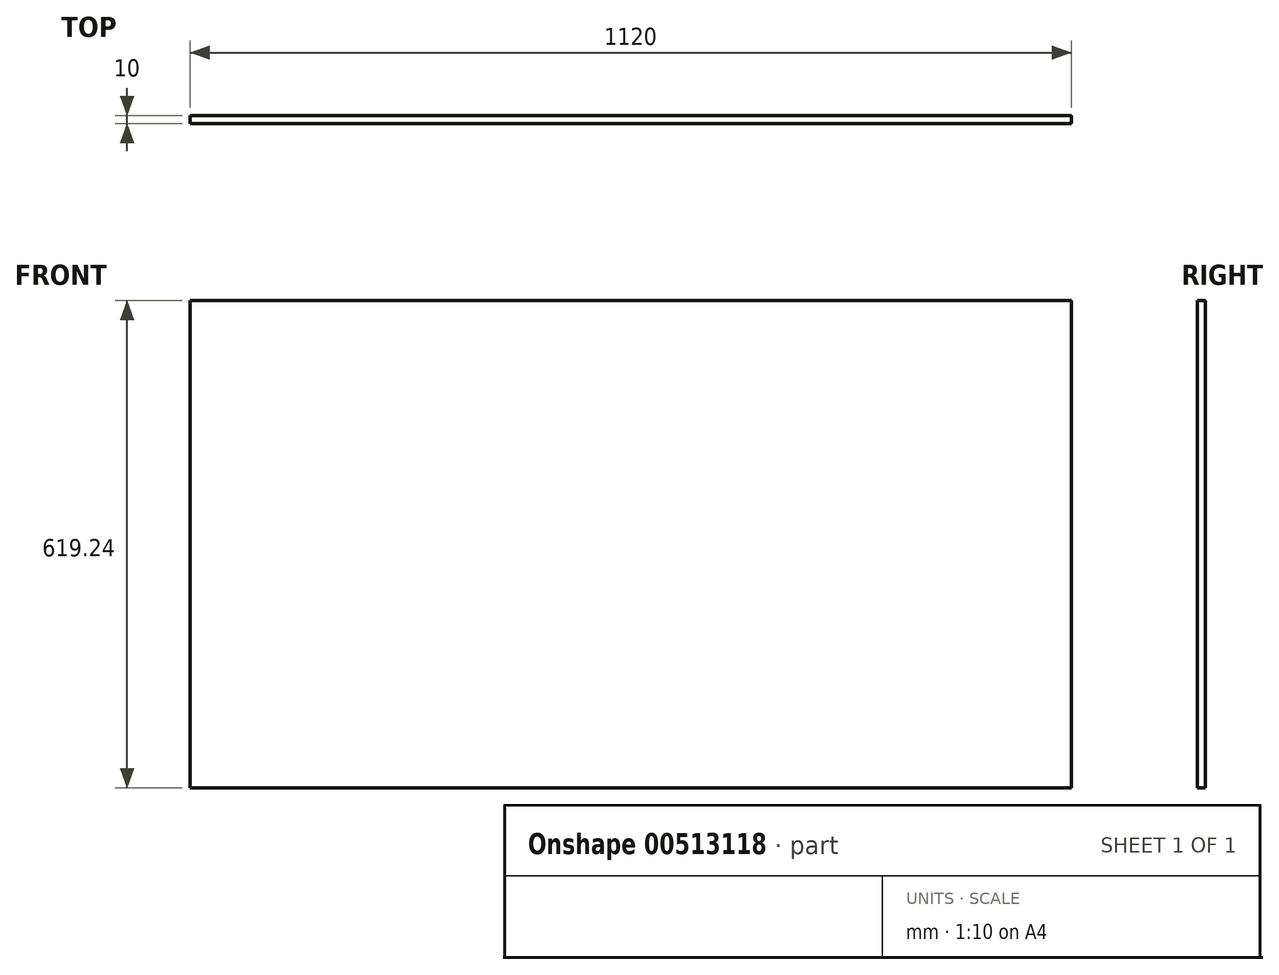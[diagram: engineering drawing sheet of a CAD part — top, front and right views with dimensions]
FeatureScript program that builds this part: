
annotation { "Feature Type Name" : "Feature", "Feature Type Description" : "" }
export const myFeature = defineFeature(function(context is Context, id is Id, definition is map)
    precondition{}
    {
        {
            var Q0;
            Q0=qCreatedBy(makeId("Front.planeOp"),FACE);
            var sketch = newSketch(context, id + "F0", { "sketchPlane" : qUnion([Q0])});
            skLineSegment(sketch, "E0.bottom", {"start": v(-635.84, -266.8) * mm, "end": v(464.16, -266.8) * mm});
            skLineSegment(sketch, "E0.top", {"start": v(-635.84, -866.04) * mm, "end": v(464.16, -866.04) * mm});
            skLineSegment(sketch, "E0.left", {"start": v(-635.84, -266.8) * mm, "end": v(-635.84, -866.04) * mm});
            skLineSegment(sketch, "E0.right", {"start": v(464.16, -266.8) * mm, "end": v(464.16, -866.04) * mm});
            skSolve(sketch);
        }
        {
            var Q0;
            Q0=makeQuery(id+"F0.imprint","IMPRINT",FACE,{"disambiguationData":[TD([[makeQuery(id+"F0.imprint","IMPRINT",EDGE,{"derivedFrom":sQuery(id+"F0.wireOp",EDGE,"E0.bottom")}),-1.0]])]});
            extrude(context, id + "F1", {"entities" : qUnion([Q0]), "depth" : 10 * mm, "offsetDistance" : 25 * mm});
        }
        {
            var Q0;
            Q0=makeQuery(id+"F1.opExtrude","SWEPT_FACE",FACE,{"disambiguationData":[OSD([sQuery(id+"F0.wireOp",EDGE,"E0.bottom")])]});
            extrude(context, id + "F2", {"entities" : qUnion([Q0]), "operationType" : NewBodyOperationType.ADD, "depth" : 10 * mm, "offsetDistance" : 25 * mm});
        }
        {
            var Q0;
            {var subQ0=sQuery(id+"F0.wireOp",EDGE,"E0.left");Q0=makeQuery(id+"F2.boolean.opBoolean","MERGE",FACE,{"derivedFrom":[makeQuery(id+"F1.opExtrude","SWEPT_FACE",FACE,{"disambiguationData":[OSD([subQ0])]}),makeQuery(id+"F2.opExtrude","SWEPT_FACE",FACE,{"disambiguationData":[OSD([sQuery(id+"F0.wireOp",EDGE,"E0.bottom"),subQ0])]})]});}
            extrude(context, id + "F3", {"entities" : qUnion([Q0]), "operationType" : NewBodyOperationType.ADD, "depth" : 10 * mm, "offsetDistance" : 25 * mm});
        }
        {
            var Q0;
            {var subQ0=sQuery(id+"F0.wireOp",EDGE,"E0.top");Q0=makeQuery(id+"F3.boolean.opBoolean","MERGE",FACE,{"derivedFrom":[makeQuery(id+"F1.opExtrude","SWEPT_FACE",FACE,{"disambiguationData":[OSD([subQ0])]}),makeQuery(id+"F3.opExtrude","SWEPT_FACE",FACE,{"disambiguationData":[OSD([subQ0,sQuery(id+"F0.wireOp",EDGE,"E0.left")])]})]});}
            extrude(context, id + "F4", {"entities" : qUnion([Q0]), "operationType" : NewBodyOperationType.ADD, "depth" : 10 * mm, "offsetDistance" : 25 * mm});
        }
        {
            var Q0;
            {var subQ0=sQuery(id+"F0.wireOp",EDGE,"E0.right");Q0=makeQuery(id+"F4.boolean.opBoolean","MERGE",FACE,{"derivedFrom":[makeQuery(id+"F2.boolean.opBoolean","MERGE",FACE,{"derivedFrom":[makeQuery(id+"F1.opExtrude","SWEPT_FACE",FACE,{"disambiguationData":[OSD([subQ0])]}),makeQuery(id+"F2.opExtrude","SWEPT_FACE",FACE,{"disambiguationData":[OSD([sQuery(id+"F0.wireOp",EDGE,"E0.bottom"),subQ0])]})]}),makeQuery(id+"F4.opExtrude","SWEPT_FACE",FACE,{"disambiguationData":[OSD([sQuery(id+"F0.wireOp",EDGE,"E0.top"),subQ0])]})]});}
            extrude(context, id + "F5", {"entities" : qUnion([Q0]), "operationType" : NewBodyOperationType.ADD, "depth" : 10 * mm, "offsetDistance" : 25 * mm});
        }
    });
